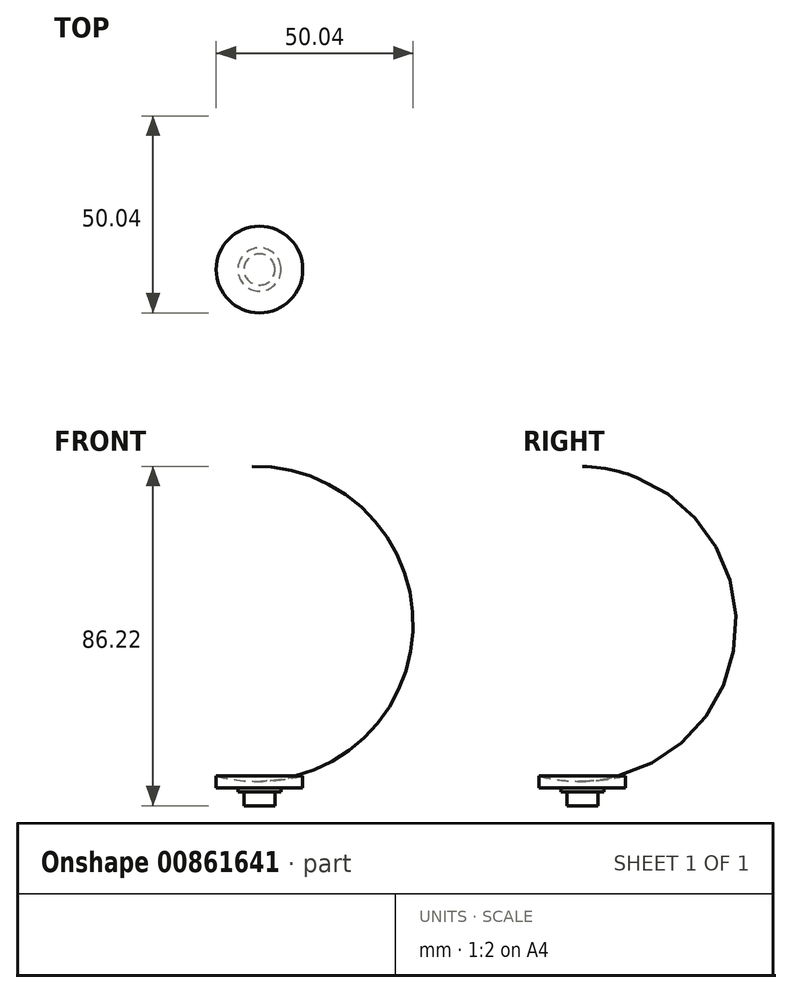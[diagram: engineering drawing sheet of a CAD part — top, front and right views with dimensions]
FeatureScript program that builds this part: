
annotation { "Feature Type Name" : "Feature", "Feature Type Description" : "" }
export const myFeature = defineFeature(function(context is Context, id is Id, definition is map)
    precondition{}
    {
        {
            var Q0;
            Q0=qCreatedBy(makeId("Front.planeOp"),FACE);
            var sketch = newSketch(context, id + "F0", { "sketchPlane" : qUnion([Q0])});
            skLineSegment(sketch, "E0", {"start": v(0, 0) * mm, "end": v(0, 6.23) * mm});
            skLineSegment(sketch, "E1", {"start": v(-11, 7.5) * mm, "end": v(-11, 4.5) * mm});
            skLineSegment(sketch, "E2", {"start": v(-11, 4.5) * mm, "end": v(-5.5, 4.5) * mm});
            skLineSegment(sketch, "E3", {"start": v(-5.5, 4.5) * mm, "end": v(-5.5, 3.5) * mm});
            skLineSegment(sketch, "E4", {"start": v(-5.5, 3.5) * mm, "end": v(-3.95, 3.5) * mm});
            skLineSegment(sketch, "E5", {"start": v(-3.95, 3.5) * mm, "end": v(-3.95, 0) * mm});
            skLineSegment(sketch, "E6", {"start": v(-3.95, 0) * mm, "end": v(0, 0) * mm});
            skArc(sketch, "E7", {"start": v(-11, 7.5) * mm, "mid": v(-5.54, 6.48) * mm, "end": v(0, 6.23) * mm});
            skSolve(sketch);
        }
        {
            var Q0;
            Q0=makeQuery(id+"F0.imprint","IMPRINT",FACE,{"disambiguationData":[TD([[makeQuery(id+"F0.imprint","IMPRINT",EDGE,{"derivedFrom":sQuery(id+"F0.wireOp",EDGE,"E0")}),1.0]])]});
            var Q1;
            Q1=sQuery(id+"F0.wireOp",EDGE,"E0");
            revolve(context, id + "F1", {"surfaceOperationType" : NewSurfaceOperationType.NEW, "entities" : qUnion([Q0]), "axis" : qUnion([Q1]), "revolveType" : RevolveType.FULL});
        }
    });
